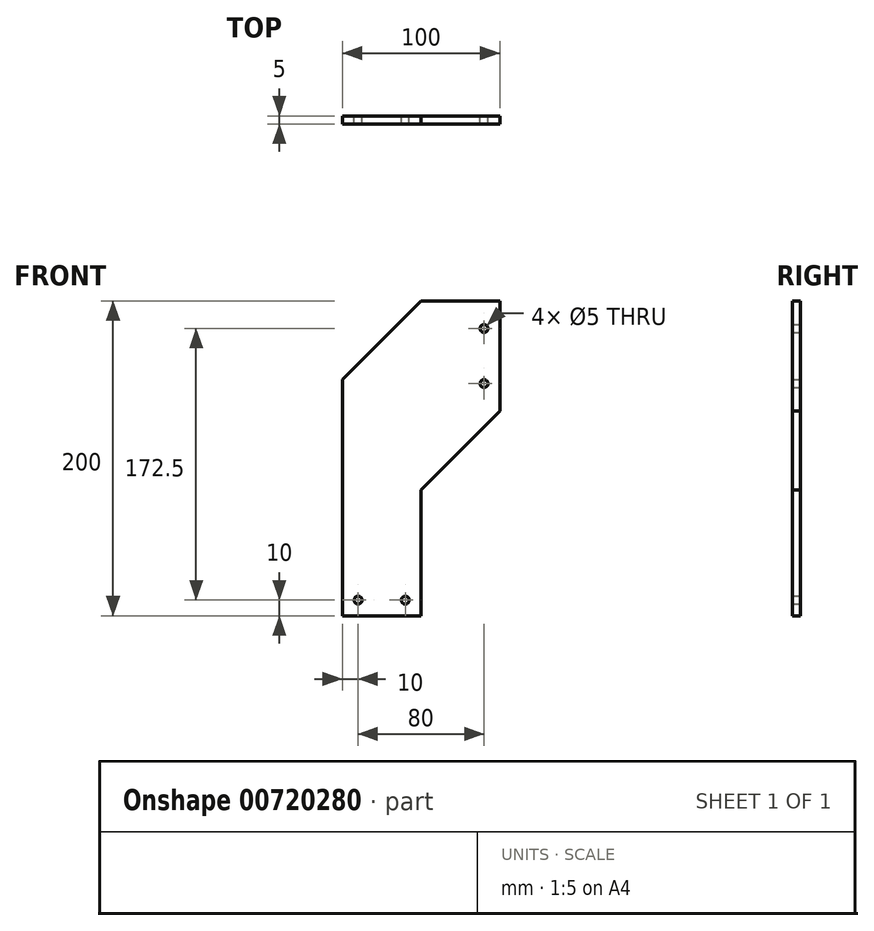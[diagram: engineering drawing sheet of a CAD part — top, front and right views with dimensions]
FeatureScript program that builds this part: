
annotation { "Feature Type Name" : "Feature", "Feature Type Description" : "" }
export const myFeature = defineFeature(function(context is Context, id is Id, definition is map)
    precondition{}
    {
        {
            var Q0;
            Q0=qCreatedBy(makeId("Front.planeOp"),FACE);
            var sketch = newSketch(context, id + "F0", { "sketchPlane" : qUnion([Q0])});
            skLineSegment(sketch, "E0.bottom", {"start": v(50, 100) * mm, "end": v(-50, 100) * mm});
            skLineSegment(sketch, "E0.top", {"start": v(50, -100) * mm, "end": v(-50, -100) * mm});
            skLineSegment(sketch, "E0.left", {"start": v(50, 100) * mm, "end": v(50, -100) * mm});
            skLineSegment(sketch, "E0.right", {"start": v(-50, 100) * mm, "end": v(-50, -100) * mm});
            skPoint(sketch, "E0.middle", {"position": v(0, 0) * mm});
            skLineSegment(sketch, "E1", {"start": v(0, -100) * mm, "end": v(0, 100) * mm});
            skLineSegment(sketch, "E2", {"start": v(-50, 30) * mm, "end": v(50, 30) * mm});
            skLineSegment(sketch, "E3", {"start": v(-50, -20) * mm, "end": v(50, -20) * mm, "construction": true});
            skLineSegment(sketch, "E4", {"start": v(-50, 50) * mm, "end": v(50, 50) * mm, "construction": true});
            skLineSegment(sketch, "E5", {"start": v(0, 100) * mm, "end": v(-50, 50) * mm});
            skLineSegment(sketch, "E6", {"start": v(50, 30) * mm, "end": v(0, -20) * mm});
            skSolve(sketch);
        }
        {
            var Q0;
            {var subQ0=sQuery(id+"F0.wireOp",EDGE,"E0.left");var subQ1=sQuery(id+"F0.wireOp",EDGE,"E0.bottom");var subQ2=makeQuery(id+"F0.imprint","INTERSECT",VERTEX,{"derivedFrom":[subQ1,subQ0]});Q0=makeQuery(id+"F0.imprint","IMPRINT",FACE,{"disambiguationData":[TD([[makeQuery(id+"F0.imprint","IMPRINT",EDGE,{"disambiguationData":[TD([[subQ2,-1.0]])],"derivedFrom":subQ1}),1.0]])]});}
            var Q1;
            {var subQ4=sQuery(id+"F0.wireOp",EDGE,"E0.top");var subQ6=sQuery(id+"F0.wireOp",EDGE,"E0.right");var subQ7=makeQuery(id+"F0.imprint","INTERSECT",VERTEX,{"derivedFrom":[subQ4,subQ6]});Q1=makeQuery(id+"F0.imprint","IMPRINT",FACE,{"disambiguationData":[TD([[makeQuery(id+"F0.imprint","IMPRINT",EDGE,{"disambiguationData":[TD([[subQ7,1.0]])],"derivedFrom":subQ4}),-1.0]])]});}
            var Q2;
            {var subQ3=sQuery(id+"F0.wireOp",EDGE,"E5");Q2=makeQuery(id+"F0.imprint","IMPRINT",FACE,{"disambiguationData":[TD([[makeQuery(id+"F0.imprint","IMPRINT",EDGE,{"derivedFrom":subQ3}),1.0]])]});}
            var Q3;
            {var subQ0=sQuery(id+"F0.wireOp",EDGE,"E6");Q3=makeQuery(id+"F0.imprint","IMPRINT",FACE,{"disambiguationData":[TD([[makeQuery(id+"F0.imprint","IMPRINT",EDGE,{"derivedFrom":subQ0}),-1.0]])]});}
            extrude(context, id + "F1", {"entities" : qUnion([Q0, Q1, Q2, Q3]), "depth" : 5 * mm, "offsetDistance" : 25 * mm});
        }
        {
            var Q0;
            Q0=makeQuery(id+"F1.opExtrude","CAP_FACE",FACE,{"disambiguationData":[OSD([sQuery(id+"F0.wireOp",EDGE,"E0.bottom"),sQuery(id+"F0.wireOp",EDGE,"E0.top"),sQuery(id+"F0.wireOp",EDGE,"E0.left"),sQuery(id+"F0.wireOp",EDGE,"E0.right"),sQuery(id+"F0.wireOp",EDGE,"E1"),sQuery(id+"F0.wireOp",EDGE,"E5"),sQuery(id+"F0.wireOp",EDGE,"E6")])],"isStart":false});
            var sketch = newSketch(context, id + "F2", { "sketchPlane" : qUnion([Q0])});
            skLineSegment(sketch, "E7", {"start": v(40, 100) * mm, "end": v(40, 20) * mm, "construction": true});
            skPoint(sketch, "E8", {"position": v(40, 82.5) * mm});
            skPoint(sketch, "E9", {"position": v(40, 47.5) * mm});
            skLineSegment(sketch, "E10", {"start": v(-50, -90) * mm, "end": v(0, -90) * mm, "construction": true});
            skPoint(sketch, "E11", {"position": v(-40, -90) * mm});
            skPoint(sketch, "E12", {"position": v(-10, -90) * mm});
            skSolve(sketch);
        }
        {
            var Q0;
            Q0=sQuery(id+"F2.wireOp",VERTEX,"E8");
            var Q1;
            Q1=sQuery(id+"F2.wireOp",VERTEX,"E9");
            var Q2;
            Q2=sQuery(id+"F2.wireOp",VERTEX,"E12");
            var Q3;
            Q3=sQuery(id+"F2.wireOp",VERTEX,"E11");
            var Q4;
            Q4=makeQuery(id+"F1.opExtrude","SWEPT_BODY",BODY,{"disambiguationData":[OSD([sQuery(id+"F0.wireOp",EDGE,"E0.bottom"),sQuery(id+"F0.wireOp",EDGE,"E0.top"),sQuery(id+"F0.wireOp",EDGE,"E0.left"),sQuery(id+"F0.wireOp",EDGE,"E0.right"),sQuery(id+"F0.wireOp",EDGE,"E1"),sQuery(id+"F0.wireOp",EDGE,"E5"),sQuery(id+"F0.wireOp",EDGE,"E6")])]});
            hole(context, id + "F3", {"style" : HoleStyle.SIMPLE, "endStyle" : HoleEndStyle.BLIND, "holeDiameter" : 5 * mm, "majorDiameter" : 5 * mm, "holeDepth" : 40 * mm, "tappedDepth" : 12 * mm, "tapClearance" : 3, "locations" : qUnion([Q0, Q1, Q2, Q3]), "scope" : qUnion([Q4])});
        }
    });
